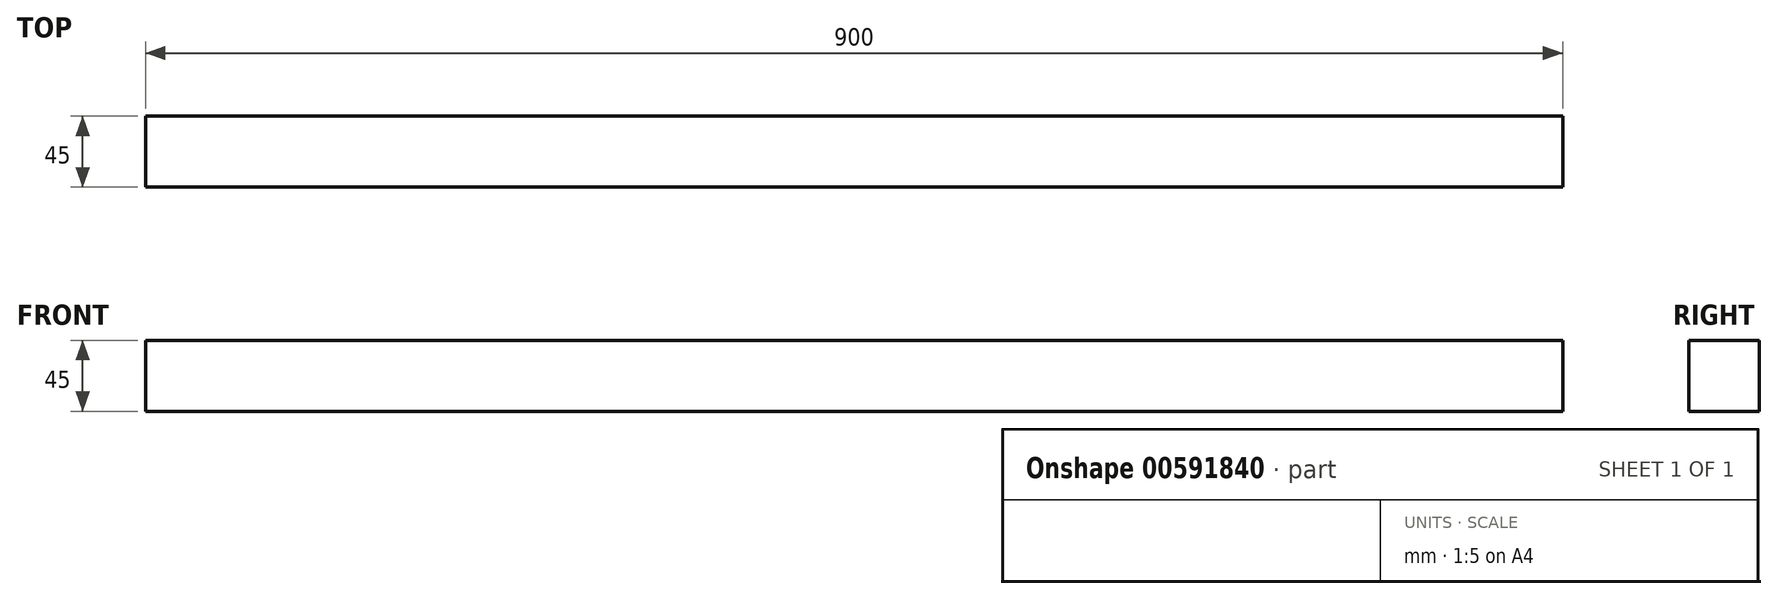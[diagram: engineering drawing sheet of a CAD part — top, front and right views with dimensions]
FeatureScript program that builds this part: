
annotation { "Feature Type Name" : "Feature", "Feature Type Description" : "" }
export const myFeature = defineFeature(function(context is Context, id is Id, definition is map)
    precondition{}
    {
        {
            var Q0;
            Q0=qCreatedBy(makeId("Right.planeOp"),FACE);
            var sketch = newSketch(context, id + "F0", { "sketchPlane" : qUnion([Q0])});
            skLineSegment(sketch, "E0.bottom", {"start": v(0, 0) * mm, "end": v(45, 0) * mm});
            skLineSegment(sketch, "E0.top", {"start": v(0, 45) * mm, "end": v(45, 45) * mm});
            skLineSegment(sketch, "E0.left", {"start": v(0, 0) * mm, "end": v(0, 45) * mm});
            skLineSegment(sketch, "E0.right", {"start": v(45, 0) * mm, "end": v(45, 45) * mm});
            skSolve(sketch);
        }
        {
            var Q0;
            Q0=makeQuery(id+"F0.imprint","IMPRINT",FACE,{"disambiguationData":[TD([[makeQuery(id+"F0.imprint","IMPRINT",EDGE,{"derivedFrom":sQuery(id+"F0.wireOp",EDGE,"E0.bottom")}),1.0]])]});
            extrude(context, id + "F1", {"entities" : qUnion([Q0]), "depth" : 900 * mm, "offsetDistance" : 25 * mm});
        }
    });
